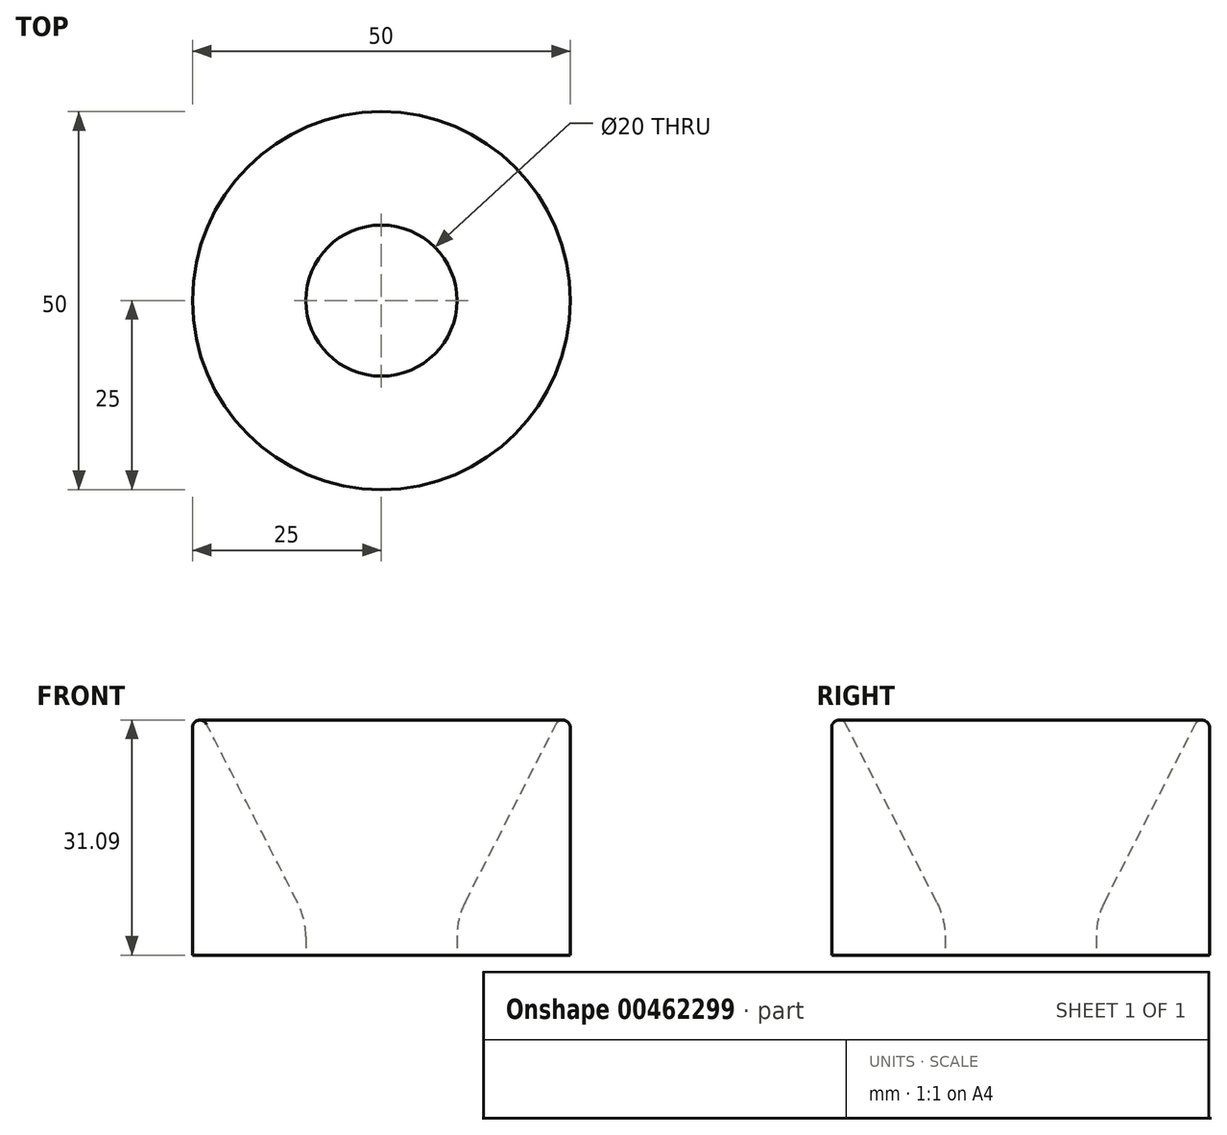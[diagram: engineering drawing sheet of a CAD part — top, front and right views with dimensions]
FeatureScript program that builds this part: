
annotation { "Feature Type Name" : "Feature", "Feature Type Description" : "" }
export const myFeature = defineFeature(function(context is Context, id is Id, definition is map)
    precondition{}
    {
        {
            var Q0;
            Q0=qCreatedBy(makeId("Front.planeOp"),FACE);
            var sketch = newSketch(context, id + "F0", { "sketchPlane" : qUnion([Q0])});
            skLineSegment(sketch, "E0", {"start": v(0, 0) * mm, "end": v(0, 27.96) * mm, "construction": true});
            skLineSegment(sketch, "E1", {"start": v(-7.25, 0) * mm, "end": v(-12.35, 10) * mm, "construction": true});
            skLineSegment(sketch, "E2", {"start": v(-25, 0) * mm, "end": v(-10, 0) * mm});
            skLineSegment(sketch, "E3", {"start": v(-11.1, 6.98) * mm, "end": v(-23.1, 30.55) * mm});
            skLineSegment(sketch, "E4", {"start": v(-25, 30.1) * mm, "end": v(-25, 0) * mm});
            skPoint(sketch, "E5.visualSharp", {"position": v(-25, 34.25) * mm});
            skArc(sketch, "E5.filletArc", {"start": v(-23.1, 30.55) * mm, "mid": v(-24.23, 31.06) * mm, "end": v(-25, 30.1) * mm});
            skLineSegment(sketch, "E6", {"start": v(-10, 2.44) * mm, "end": v(-10, 0) * mm});
            skPoint(sketch, "E7.visualSharp", {"position": v(-10, 4.84) * mm});
            skArc(sketch, "E7.filletArc", {"start": v(-10, 2.44) * mm, "mid": v(-10.28, 4.78) * mm, "end": v(-11.1, 6.98) * mm});
            skSolve(sketch);
        }
        {
            var Q0;
            Q0=makeQuery(id+"F0.imprint","IMPRINT",FACE,{"disambiguationData":[TD([[makeQuery(id+"F0.imprint","IMPRINT",EDGE,{"derivedFrom":sQuery(id+"F0.wireOp",EDGE,"E2")}),1.0]])]});
            var Q1;
            Q1=sQuery(id+"F0.wireOp",EDGE,"E0");
            revolve(context, id + "F1", {"entities" : qUnion([Q0]), "axis" : qUnion([Q1]), "revolveType" : RevolveType.FULL});
        }
    });
